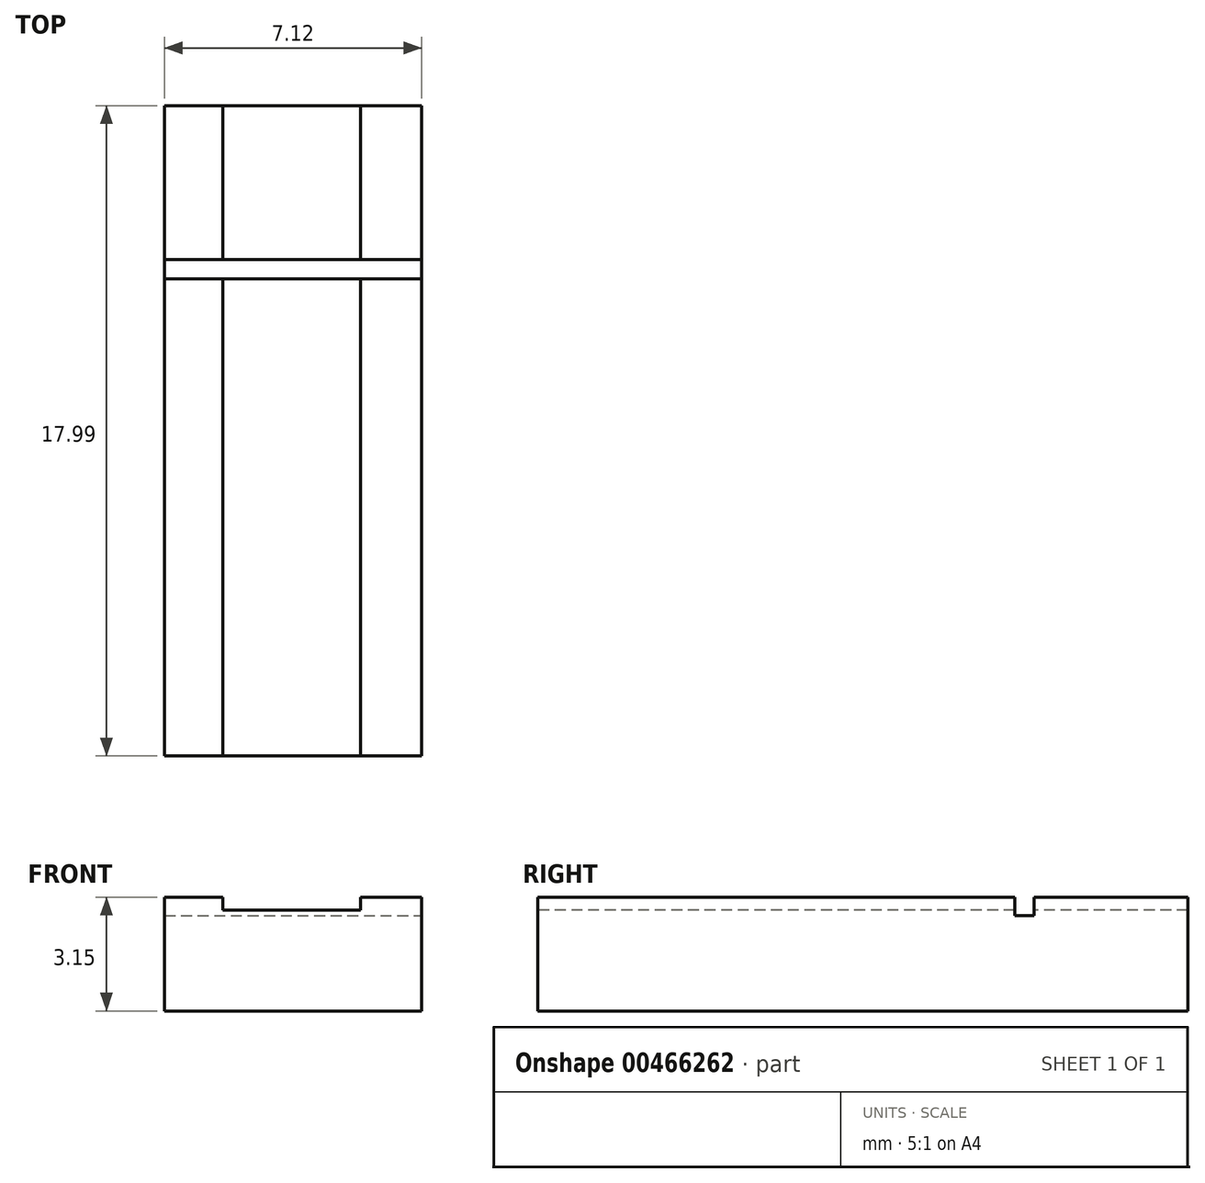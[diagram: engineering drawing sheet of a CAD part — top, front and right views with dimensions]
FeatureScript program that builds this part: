
annotation { "Feature Type Name" : "Feature", "Feature Type Description" : "" }
export const myFeature = defineFeature(function(context is Context, id is Id, definition is map)
    precondition{}
    {
        {
            var Q0;
            Q0=qCreatedBy(makeId("Top.planeOp"),FACE);
            var sketch = newSketch(context, id + "F0", { "sketchPlane" : qUnion([Q0])});
            skLineSegment(sketch, "E0.bottom", {"start": v(-4.19, 8.6) * mm, "end": v(2.93, 8.6) * mm});
            skLineSegment(sketch, "E0.top", {"start": v(-4.19, -9.39) * mm, "end": v(2.93, -9.39) * mm});
            skLineSegment(sketch, "E0.left", {"start": v(-4.19, 8.6) * mm, "end": v(-4.19, -9.39) * mm});
            skLineSegment(sketch, "E0.right", {"start": v(2.93, 8.6) * mm, "end": v(2.93, -9.39) * mm});
            skLineSegment(sketch, "E1.bottom", {"start": v(-2.57, 9.89) * mm, "end": v(1.24, 9.89) * mm});
            skLineSegment(sketch, "E1.top", {"start": v(-2.57, -10.92) * mm, "end": v(1.24, -10.92) * mm});
            skLineSegment(sketch, "E1.left", {"start": v(-2.57, 9.89) * mm, "end": v(-2.57, -10.92) * mm});
            skLineSegment(sketch, "E1.right", {"start": v(1.24, 9.89) * mm, "end": v(1.24, -10.92) * mm});
            skSolve(sketch);
        }
        {
            var Q0;
            Q0=makeQuery(id+"F0.imprint","IMPRINT",FACE,{"disambiguationData":[TD([[makeQuery(id+"F0.imprint","IMPRINT",EDGE,{"derivedFrom":sQuery(id+"F0.wireOp",EDGE,"E0.bottom")}),-1.0]])]});
            extrude(context, id + "F1", {"entities" : qUnion([Q0]), "depth" : 3.15 * mm});
        }
        {
            var Q0;
            {var subQ0=sQuery(id+"F0.wireOp",EDGE,"E1.left");var subQ1=sQuery(id+"F0.wireOp",EDGE,"E0.bottom");var subQ2=makeQuery(id+"F0.imprint","INTERSECT",VERTEX,{"derivedFrom":[subQ1,subQ0]});Q0=makeQuery(id+"F0.imprint","IMPRINT",FACE,{"disambiguationData":[TD([[makeQuery(id+"F0.imprint","IMPRINT",EDGE,{"disambiguationData":[TD([[subQ2,-1.0]])],"derivedFrom":subQ1}),-1.0]])]});}
            extrude(context, id + "F2", {"entities" : qUnion([Q0]), "operationType" : NewBodyOperationType.REMOVE, "depth" : 4.88 * mm, "hasSecondDirection" : true, "secondDirectionOppositeDirection" : false, "secondDirectionDepth" : 2.8 * mm});
        }
        {
            var Q0;
            {var subQ0=sQuery(id+"F0.wireOp",EDGE,"E0.bottom");var subQ1=sQuery(id+"F0.wireOp",EDGE,"E0.top");var subQ2=sQuery(id+"F0.wireOp",EDGE,"E0.left");Q0=makeQuery(id+"F2.boolean.opBoolean","SPLIT",FACE,{"disambiguationData":[TD([makeQuery(id+"F1.opExtrude","SWEPT_FACE",FACE,{"disambiguationData":[OSD([subQ2])]})])],"derivedFrom":makeQuery(id+"F1.opExtrude","CAP_FACE",FACE,{"disambiguationData":[OSD([subQ0,subQ1,subQ2,sQuery(id+"F0.wireOp",EDGE,"E0.right")])],"isStart":false})});}
            var sketch = newSketch(context, id + "F3", { "sketchPlane" : qUnion([Q0])});
            skLineSegment(sketch, "E2.bottom", {"start": v(-6.65, 4.35) * mm, "end": v(6.05, 4.35) * mm});
            skLineSegment(sketch, "E2.top", {"start": v(-6.65, 3.82) * mm, "end": v(6.05, 3.82) * mm});
            skLineSegment(sketch, "E2.left", {"start": v(-6.65, 4.35) * mm, "end": v(-6.65, 3.82) * mm});
            skLineSegment(sketch, "E2.right", {"start": v(6.05, 4.35) * mm, "end": v(6.05, 3.82) * mm});
            skSolve(sketch);
        }
        {
            var Q0;
            {var subQ0=sQuery(id+"F3.wireOp",EDGE,"E2.right");Q0=makeQuery(id+"F3.imprint","IMPRINT",FACE,{"disambiguationData":[TD([[makeQuery(id+"F3.imprint","IMPRINT",EDGE,{"derivedFrom":subQ0}),-1.0]])]});}
            var Q1;
            {var subQ0=sQuery(id+"F3.wireOp",EDGE,"E2.bottom");var subQ1=sQuery(id+"F0.wireOp",EDGE,"E0.left");var subQ2=makeQuery(id+"F1.opExtrude","CAP_EDGE",EDGE,{"disambiguationData":[OSD([subQ1])],"isStart":false});var subQ3=makeQuery(id+"F3.imprint","INTERSECT",VERTEX,{"derivedFrom":[subQ2,subQ0]});Q1=makeQuery(id+"F3.imprint","IMPRINT",FACE,{"disambiguationData":[TD([[makeQuery(id+"F3.imprint","IMPRINT",EDGE,{"disambiguationData":[TD([[subQ3,-1.0]])],"derivedFrom":subQ2}),1.0]])]});}
            extrude(context, id + "F4", {"entities" : qUnion([Q0, Q1]), "operationType" : NewBodyOperationType.REMOVE, "oppositeDirection" : true, "depth" : 0.5 * mm});
        }
    });
